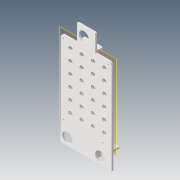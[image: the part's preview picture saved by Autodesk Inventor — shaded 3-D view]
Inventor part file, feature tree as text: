
AUTODESK INVENTOR PART (.ipt)
format: ipt  version: 2022 (Build 260153000, 153)  size: 257,024 bytes
history: native  units: mm
features: reference x11, other x7, extrude x4, sketch x4, plane x2, pattern_linear x1, projected_geometry x1
ambient origin geometry x8: Origin, YZ Plane, XZ Plane, XY Plane, X Axis, Y Axis, Z Axis, Center Point
bodies: Volumenkörper1 (feature_tree)
feature tree (30):
  plane  "Arbeitsebene1"
  extrude  "Extrusion1"  Depth=3.0mm
  extrude  "Extrusion2"  Depth=60.0mm
  pattern_linear  "Rechteckige Anordnung1"  Count1=4 Spacing1=18.9mm
  sketch  "Skizze3"  dims[d11=2.0mm d12=0.0mm d13=3.0mm]
  plane  "Arbeitsebene2"
  extrude  "Extrusion3"  Depth=3.0mm
  extrude  "Extrusion4"  Depth=10.0mm TaperAngle=0.0deg
  sketch  "Skizze1"  dims[d0=3.0mm d1=0.0mm d2=7.0mm]
  reference  "Referenz1"
  sketch  "Skizze2"  dims[d3=0.0mm d4=0.0mm d5=60.0mm d7=18.9mm d8=40.0mm d10=18.9mm]
  reference  "Referenz2"
  reference  "Referenz3"
  reference  "Referenz4"
  reference  "Referenz5"
  projected_geometry  "Projizierte Kontur1"
  sketch  "Skizze4"  dims[d14=3.0mm d15=10.0mm d16=0.0mm d17=3.0mm d18=3.0mm]
  reference  "Referenz6"
  reference  "Referenz7"
  reference  "Referenz8"
  reference  "Referenz9"
  reference  "Referenz10"
  reference  "Referenz11"
  other  "Omniscope_new_v0.iam"
  other  "Omniscope_sidewalls_v0:1"
  other  "OV_Camera:1"
  other  "00_Z_Focus_CCTV_Camera:1"
  other  "00_Z_Focus_CCTV_Camera:3"
  other  "00_Z_Focus_CCTV_Camera:2"
  other  "Omniscope_sidewall_spacer_v0:1"
